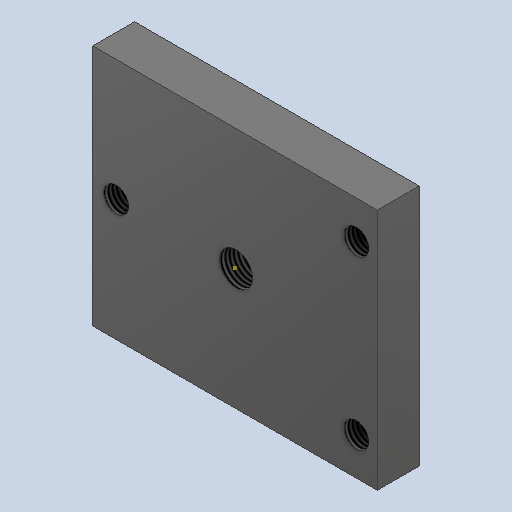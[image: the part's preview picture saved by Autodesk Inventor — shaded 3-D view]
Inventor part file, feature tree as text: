
AUTODESK INVENTOR PART (.ipt)
format: ipt  version: 2025.1 (Build 291241000, 241)  size: 124,928 bytes
history: native  units: in
note: dims shown in document units (in); Inventor stores cm internally (conversion verified against a paired STEP export)
features: sketch x4, other x3
ambient origin geometry x8: Origin, YZ Plane, XZ Plane, XY Plane, X Axis, Y Axis, Z Axis, Center Point
bodies: Solid1 (feature_tree)
feature tree (7):
  other  "Part2.ipt"
  other  "Solid1::Part2.ipt"
  other  "TaggingFeature1"
  sketch  "Sketch1"  dims[d0=0.3937in]
  sketch  "Sketch2"
  sketch  "Sketch3"
  sketch  "Sketch4"
